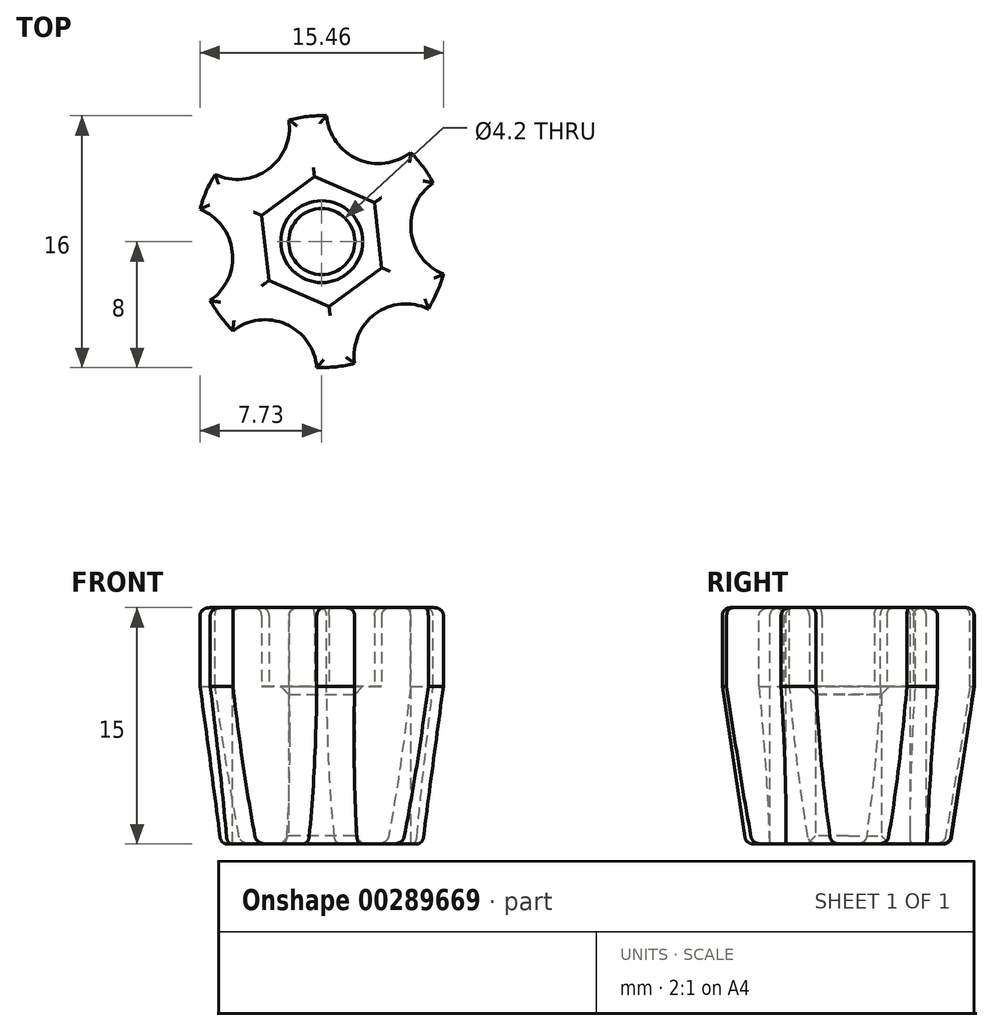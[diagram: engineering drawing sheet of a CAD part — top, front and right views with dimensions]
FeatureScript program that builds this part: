
annotation { "Feature Type Name" : "Feature", "Feature Type Description" : "" }
export const myFeature = defineFeature(function(context is Context, id is Id, definition is map)
    precondition{}
    {
        {
            var Q0;
            Q0=qCreatedBy(makeId("Top.planeOp"),FACE);
            var sketch = newSketch(context, id + "F0", { "sketchPlane" : qUnion([Q0])});
            skCircle(sketch, "E0", {"center": v(0, 0) * mm, "radius": 2.1 * mm});
            skCircle(sketch, "E1", {"center": v(0, 0) * mm, "radius": 6 * mm});
            skSolve(sketch);
        }
        {
            var Q0;
            Q0=makeQuery(id+"F0.imprint","IMPRINT",FACE,{"disambiguationData":[TD([[makeQuery(id+"F0.imprint","IMPRINT",EDGE,{"derivedFrom":sQuery(id+"F0.wireOp",EDGE,"E0")}),-1.0]])]});
            extrude(context, id + "F1", {"entities" : qUnion([Q0]), "depth" : 10 * mm});
        }
        {
            var Q0;
            Q0=qCreatedBy(makeId("Front.planeOp"),FACE);
            var sketch = newSketch(context, id + "F2", { "sketchPlane" : qUnion([Q0])});
            skLineSegment(sketch, "E2", {"start": v(0, 10) * mm, "end": v(0, 20) * mm});
            skLineSegment(sketch, "E3", {"start": v(0, 20) * mm, "end": v(8, 20) * mm});
            skLineSegment(sketch, "E4", {"start": v(8, 20) * mm, "end": v(0, 10) * mm});
            skLineSegment(sketch, "E5", {"start": v(0, 10) * mm, "end": v(6.5, 10) * mm});
            skLineSegment(sketch, "E6", {"start": v(6.5, 10) * mm, "end": v(8, 20) * mm});
            skLineSegment(sketch, "E7", {"start": v(0, 20) * mm, "end": v(2.1, 20) * mm});
            skLineSegment(sketch, "E8", {"start": v(2.1, 20) * mm, "end": v(2.1, 10) * mm});
            skSolve(sketch);
        }
        {
            var Q0;
            {var subQ0=sQuery(id+"F2.wireOp",EDGE,"E3");Q0=makeQuery(id+"F2.imprint","IMPRINT",FACE,{"disambiguationData":[TD([[makeQuery(id+"F2.imprint","IMPRINT",EDGE,{"derivedFrom":subQ0}),-1.0]])]});}
            var Q1;
            {var subQ0=sQuery(id+"F2.wireOp",EDGE,"E6");Q1=makeQuery(id+"F2.imprint","IMPRINT",FACE,{"disambiguationData":[TD([[makeQuery(id+"F2.imprint","IMPRINT",EDGE,{"derivedFrom":subQ0}),1.0]])]});}
            var Q2;
            Q2=sQuery(id+"F2.wireOp",EDGE,"E2");
            revolve(context, id + "F3", {"operationType" : NewBodyOperationType.ADD, "entities" : qUnion([Q0, Q1]), "axis" : qUnion([Q2]), "revolveType" : RevolveType.FULL});
        }
        {
            var Q0;
            Q0=makeQuery(id+"F3.opRevolve","SWEPT_FACE",FACE,{"disambiguationData":[OSD([sQuery(id+"F2.wireOp",EDGE,"E3")])]});
            var sketch = newSketch(context, id + "F4", { "sketchPlane" : qUnion([Q0])});
            skCircle(sketch, "E9.cCircle", {"center": v(0, 0) * mm, "radius": 5.25 * mm, "construction": true});
            skLineSegment(sketch, "E9.0", {"start": v(5.56, -2.42) * mm, "end": v(0.68, -6.02) * mm});
            skLineSegment(sketch, "E9.1", {"start": v(0.68, -6.02) * mm, "end": v(-4.88, -3.6) * mm});
            skLineSegment(sketch, "E9.2", {"start": v(-4.88, -3.6) * mm, "end": v(-5.56, 2.42) * mm});
            skLineSegment(sketch, "E9.3", {"start": v(-5.56, 2.42) * mm, "end": v(-0.68, 6.02) * mm});
            skLineSegment(sketch, "E9.4", {"start": v(-0.68, 6.02) * mm, "end": v(4.88, 3.6) * mm});
            skLineSegment(sketch, "E9.5", {"start": v(4.88, 3.6) * mm, "end": v(5.56, -2.42) * mm});
            skPoint(sketch, "E9.0.midPoint", {"position": v(3.12, -4.22) * mm});
            skCircle(sketch, "E10.cCircle", {"center": v(0, 0) * mm, "radius": 3.6 * mm, "construction": true});
            skLineSegment(sketch, "E10.0", {"start": v(-3.81, 1.66) * mm, "end": v(-0.47, 4.13) * mm});
            skLineSegment(sketch, "E10.1", {"start": v(-0.47, 4.13) * mm, "end": v(3.34, 2.47) * mm});
            skLineSegment(sketch, "E10.2", {"start": v(3.34, 2.47) * mm, "end": v(3.81, -1.66) * mm});
            skLineSegment(sketch, "E10.3", {"start": v(3.81, -1.66) * mm, "end": v(0.47, -4.13) * mm});
            skLineSegment(sketch, "E10.4", {"start": v(0.47, -4.13) * mm, "end": v(-3.34, -2.47) * mm});
            skLineSegment(sketch, "E10.5", {"start": v(-3.34, -2.47) * mm, "end": v(-3.81, 1.66) * mm});
            skPoint(sketch, "E10.0.midPoint", {"position": v(-2.14, 2.9) * mm});
            skSolve(sketch);
        }
        {
            var Q0;
            Q0=makeQuery(id+"F4.imprint","IMPRINT",FACE,{"disambiguationData":[TD([[makeQuery(id+"F4.imprint","IMPRINT",EDGE,{"derivedFrom":sQuery(id+"F4.wireOp",EDGE,"E9.0")}),1.0]])]});
            var Q1;
            Q1=makeQuery(id+"F4.imprint","IMPRINT",FACE,{"disambiguationData":[TD([[makeQuery(id+"F4.imprint","IMPRINT",EDGE,{"derivedFrom":sQuery(id+"F4.wireOp",EDGE,"E9.0")}),-1.0]])]});
            extrude(context, id + "F5", {"entities" : qUnion([Q0, Q1]), "operationType" : NewBodyOperationType.ADD, "depth" : 15 * mm});
        }
        {
            var Q0;
            Q0=makeQuery(id+"F5.opExtrude","CAP_FACE",FACE,{"disambiguationData":[OSD([sQuery(id+"F2.wireOp",EDGE,"E3"),sQuery(id+"F2.wireOp",EDGE,"E4"),sQuery(id+"F2.wireOp",EDGE,"E6"),sQuery(id+"F4.wireOp",EDGE,"E9.0"),sQuery(id+"F4.wireOp",EDGE,"E9.1"),sQuery(id+"F4.wireOp",EDGE,"E9.2"),sQuery(id+"F4.wireOp",EDGE,"E9.3"),sQuery(id+"F4.wireOp",EDGE,"E9.4"),sQuery(id+"F4.wireOp",EDGE,"E9.5")])],"isStart":false});
            var sketch = newSketch(context, id + "F6", { "sketchPlane" : qUnion([Q0])});
            skArc(sketch, "E11", {"start": v(1.44, 3.3) * mm, "mid": v(-0.92, 8.13) * mm, "end": v(-2.14, 2.9) * mm});
            skArc(sketch, "E12", {"start": v(-2.14, 2.9) * mm, "mid": v(-7.5, 3.27) * mm, "end": v(-3.58, -0.4) * mm});
            skArc(sketch, "E13", {"start": v(-6.77, 4.27) * mm, "mid": v(-3.4, 4.6) * mm, "end": v(-2.09, 7.72) * mm});
            skArc(sketch, "E14", {"start": v(-1.44, -3.3) * mm, "mid": v(0.92, -8.13) * mm, "end": v(2.14, -2.9) * mm});
            skArc(sketch, "E15", {"start": v(-3.58, -0.4) * mm, "mid": v(-6.58, -4.86) * mm, "end": v(-1.44, -3.3) * mm});
            skArc(sketch, "E16", {"start": v(2.14, -2.9) * mm, "mid": v(7.5, -3.27) * mm, "end": v(3.58, 0.4) * mm});
            skArc(sketch, "E17", {"start": v(3.58, 0.4) * mm, "mid": v(6.58, 4.86) * mm, "end": v(1.44, 3.3) * mm});
            skArc(sketch, "E18", {"start": v(0.32, 8) * mm, "mid": v(2.29, 5.24) * mm, "end": v(5.64, 5.67) * mm});
            skArc(sketch, "E19", {"start": v(7.08, 3.72) * mm, "mid": v(5.68, 0.64) * mm, "end": v(7.73, -2.05) * mm});
            skArc(sketch, "E20", {"start": v(6.77, -4.27) * mm, "mid": v(3.4, -4.6) * mm, "end": v(2.09, -7.72) * mm});
            skArc(sketch, "E21", {"start": v(-0.32, -8) * mm, "mid": v(-2.29, -5.24) * mm, "end": v(-5.64, -5.67) * mm});
            skArc(sketch, "E22", {"start": v(-7.08, -3.72) * mm, "mid": v(-5.68, -0.64) * mm, "end": v(-7.73, 2.05) * mm});
            skSolve(sketch);
        }
        {
            var Q0;
            {var subQ0=sQuery(id+"F6.wireOp",EDGE,"E13");var subQ1=sQuery(id+"F6.wireOp",EDGE,"E11");var subQ4=makeQuery(id+"F6.imprint","INTERSECT",VERTEX,{"derivedFrom":[subQ1,subQ0]});Q0=makeQuery(id+"F6.imprint","IMPRINT",FACE,{"disambiguationData":[TD([[makeQuery(id+"F6.imprint","IMPRINT",EDGE,{"disambiguationData":[TD([[subQ4,1.0]])],"derivedFrom":subQ0}),1.0]])]});}
            var Q1;
            {var subQ0=sQuery(id+"F6.wireOp",EDGE,"E13");var subQ1=sQuery(id+"F6.wireOp",EDGE,"E12");var subQ3=makeQuery(id+"F6.imprint","INTERSECT",VERTEX,{"derivedFrom":[subQ1,subQ0]});Q1=makeQuery(id+"F6.imprint","IMPRINT",FACE,{"disambiguationData":[TD([[makeQuery(id+"F6.imprint","IMPRINT",EDGE,{"disambiguationData":[TD([[subQ3,-1.0]])],"derivedFrom":subQ1}),1.0]])]});}
            var Q2;
            {var subQ0=sQuery(id+"F6.wireOp",EDGE,"E13");var subQ1=sQuery(id+"F6.wireOp",EDGE,"E11");var subQ3=makeQuery(id+"F6.imprint","INTERSECT",VERTEX,{"derivedFrom":[subQ1,subQ0]});Q2=makeQuery(id+"F6.imprint","IMPRINT",FACE,{"disambiguationData":[TD([[makeQuery(id+"F6.imprint","IMPRINT",EDGE,{"disambiguationData":[TD([[subQ3,1.0]])],"derivedFrom":subQ1}),1.0]])]});}
            var Q3;
            {var subQ0=sQuery(id+"F6.wireOp",EDGE,"E22");var subQ1=sQuery(id+"F6.wireOp",EDGE,"E12");var subQ4=makeQuery(id+"F6.imprint","INTERSECT",VERTEX,{"derivedFrom":[subQ1,subQ0]});Q3=makeQuery(id+"F6.imprint","IMPRINT",FACE,{"disambiguationData":[TD([[makeQuery(id+"F6.imprint","IMPRINT",EDGE,{"disambiguationData":[TD([[subQ4,1.0]])],"derivedFrom":subQ0}),1.0]])]});}
            var Q4;
            {var subQ0=sQuery(id+"F6.wireOp",EDGE,"E22");var subQ1=sQuery(id+"F6.wireOp",EDGE,"E12");var subQ3=makeQuery(id+"F6.imprint","INTERSECT",VERTEX,{"derivedFrom":[subQ1,subQ0]});Q4=makeQuery(id+"F6.imprint","IMPRINT",FACE,{"disambiguationData":[TD([[makeQuery(id+"F6.imprint","IMPRINT",EDGE,{"disambiguationData":[TD([[subQ3,1.0]])],"derivedFrom":subQ1}),1.0]])]});}
            var Q5;
            {var subQ0=sQuery(id+"F6.wireOp",EDGE,"E22");var subQ1=sQuery(id+"F6.wireOp",EDGE,"E15");var subQ3=makeQuery(id+"F6.imprint","INTERSECT",VERTEX,{"derivedFrom":[subQ1,subQ0]});Q5=makeQuery(id+"F6.imprint","IMPRINT",FACE,{"disambiguationData":[TD([[makeQuery(id+"F6.imprint","IMPRINT",EDGE,{"disambiguationData":[TD([[subQ3,-1.0]])],"derivedFrom":subQ1}),1.0]])]});}
            var Q6;
            {var subQ0=sQuery(id+"F6.wireOp",EDGE,"E21");var subQ1=sQuery(id+"F6.wireOp",EDGE,"E14");var subQ4=makeQuery(id+"F6.imprint","INTERSECT",VERTEX,{"derivedFrom":[subQ1,subQ0]});Q6=makeQuery(id+"F6.imprint","IMPRINT",FACE,{"disambiguationData":[TD([[makeQuery(id+"F6.imprint","IMPRINT",EDGE,{"disambiguationData":[TD([[subQ4,-1.0]])],"derivedFrom":subQ0}),1.0]])]});}
            var Q7;
            {var subQ0=sQuery(id+"F6.wireOp",EDGE,"E21");var subQ1=sQuery(id+"F6.wireOp",EDGE,"E15");var subQ3=makeQuery(id+"F6.imprint","INTERSECT",VERTEX,{"derivedFrom":[subQ1,subQ0]});Q7=makeQuery(id+"F6.imprint","IMPRINT",FACE,{"disambiguationData":[TD([[makeQuery(id+"F6.imprint","IMPRINT",EDGE,{"disambiguationData":[TD([[subQ3,1.0]])],"derivedFrom":subQ1}),1.0]])]});}
            var Q8;
            {var subQ0=sQuery(id+"F6.wireOp",EDGE,"E21");var subQ1=sQuery(id+"F6.wireOp",EDGE,"E14");var subQ3=makeQuery(id+"F6.imprint","INTERSECT",VERTEX,{"derivedFrom":[subQ1,subQ0]});Q8=makeQuery(id+"F6.imprint","IMPRINT",FACE,{"disambiguationData":[TD([[makeQuery(id+"F6.imprint","IMPRINT",EDGE,{"disambiguationData":[TD([[subQ3,-1.0]])],"derivedFrom":subQ1}),1.0]])]});}
            var Q9;
            {var subQ0=sQuery(id+"F6.wireOp",EDGE,"E20");var subQ1=sQuery(id+"F6.wireOp",EDGE,"E14");var subQ4=makeQuery(id+"F6.imprint","INTERSECT",VERTEX,{"derivedFrom":[subQ1,subQ0]});Q9=makeQuery(id+"F6.imprint","IMPRINT",FACE,{"disambiguationData":[TD([[makeQuery(id+"F6.imprint","IMPRINT",EDGE,{"disambiguationData":[TD([[subQ4,1.0]])],"derivedFrom":subQ0}),1.0]])]});}
            var Q10;
            {var subQ0=sQuery(id+"F6.wireOp",EDGE,"E20");var subQ1=sQuery(id+"F6.wireOp",EDGE,"E16");var subQ3=makeQuery(id+"F6.imprint","INTERSECT",VERTEX,{"derivedFrom":[subQ1,subQ0]});Q10=makeQuery(id+"F6.imprint","IMPRINT",FACE,{"disambiguationData":[TD([[makeQuery(id+"F6.imprint","IMPRINT",EDGE,{"disambiguationData":[TD([[subQ3,-1.0]])],"derivedFrom":subQ1}),1.0]])]});}
            var Q11;
            {var subQ0=sQuery(id+"F6.wireOp",EDGE,"E20");var subQ1=sQuery(id+"F6.wireOp",EDGE,"E14");var subQ3=makeQuery(id+"F6.imprint","INTERSECT",VERTEX,{"derivedFrom":[subQ1,subQ0]});Q11=makeQuery(id+"F6.imprint","IMPRINT",FACE,{"disambiguationData":[TD([[makeQuery(id+"F6.imprint","IMPRINT",EDGE,{"disambiguationData":[TD([[subQ3,1.0]])],"derivedFrom":subQ1}),1.0]])]});}
            var Q12;
            {var subQ0=sQuery(id+"F6.wireOp",EDGE,"E19");var subQ1=sQuery(id+"F6.wireOp",EDGE,"E16");var subQ4=makeQuery(id+"F6.imprint","INTERSECT",VERTEX,{"derivedFrom":[subQ1,subQ0]});Q12=makeQuery(id+"F6.imprint","IMPRINT",FACE,{"disambiguationData":[TD([[makeQuery(id+"F6.imprint","IMPRINT",EDGE,{"disambiguationData":[TD([[subQ4,1.0]])],"derivedFrom":subQ0}),1.0]])]});}
            var Q13;
            {var subQ0=sQuery(id+"F6.wireOp",EDGE,"E19");var subQ1=sQuery(id+"F6.wireOp",EDGE,"E16");var subQ3=makeQuery(id+"F6.imprint","INTERSECT",VERTEX,{"derivedFrom":[subQ1,subQ0]});Q13=makeQuery(id+"F6.imprint","IMPRINT",FACE,{"disambiguationData":[TD([[makeQuery(id+"F6.imprint","IMPRINT",EDGE,{"disambiguationData":[TD([[subQ3,1.0]])],"derivedFrom":subQ1}),1.0]])]});}
            var Q14;
            {var subQ0=sQuery(id+"F6.wireOp",EDGE,"E19");var subQ1=sQuery(id+"F6.wireOp",EDGE,"E17");var subQ3=makeQuery(id+"F6.imprint","INTERSECT",VERTEX,{"derivedFrom":[subQ1,subQ0]});Q14=makeQuery(id+"F6.imprint","IMPRINT",FACE,{"disambiguationData":[TD([[makeQuery(id+"F6.imprint","IMPRINT",EDGE,{"disambiguationData":[TD([[subQ3,-1.0]])],"derivedFrom":subQ1}),1.0]])]});}
            var Q15;
            {var subQ0=sQuery(id+"F6.wireOp",EDGE,"E18");var subQ1=sQuery(id+"F6.wireOp",EDGE,"E11");var subQ4=makeQuery(id+"F6.imprint","INTERSECT",VERTEX,{"derivedFrom":[subQ1,subQ0]});Q15=makeQuery(id+"F6.imprint","IMPRINT",FACE,{"disambiguationData":[TD([[makeQuery(id+"F6.imprint","IMPRINT",EDGE,{"disambiguationData":[TD([[subQ4,-1.0]])],"derivedFrom":subQ0}),1.0]])]});}
            var Q16;
            {var subQ0=sQuery(id+"F6.wireOp",EDGE,"E18");var subQ1=sQuery(id+"F6.wireOp",EDGE,"E11");var subQ3=makeQuery(id+"F6.imprint","INTERSECT",VERTEX,{"derivedFrom":[subQ1,subQ0]});Q16=makeQuery(id+"F6.imprint","IMPRINT",FACE,{"disambiguationData":[TD([[makeQuery(id+"F6.imprint","IMPRINT",EDGE,{"disambiguationData":[TD([[subQ3,-1.0]])],"derivedFrom":subQ1}),1.0]])]});}
            var Q17;
            {var subQ0=sQuery(id+"F6.wireOp",EDGE,"E18");var subQ1=sQuery(id+"F6.wireOp",EDGE,"E17");var subQ3=makeQuery(id+"F6.imprint","INTERSECT",VERTEX,{"derivedFrom":[subQ1,subQ0]});Q17=makeQuery(id+"F6.imprint","IMPRINT",FACE,{"disambiguationData":[TD([[makeQuery(id+"F6.imprint","IMPRINT",EDGE,{"disambiguationData":[TD([[subQ3,1.0]])],"derivedFrom":subQ1}),1.0]])]});}
            extrude(context, id + "F7", {"entities" : qUnion([Q0, Q1, Q2, Q3, Q4, Q5, Q6, Q7, Q8, Q9, Q10, Q11, Q12, Q13, Q14, Q15, Q16, Q17]), "operationType" : NewBodyOperationType.REMOVE, "oppositeDirection" : true, "depth" : 25 * mm});
        }
        {
            var Q0;
            Q0=makeQuery(id+"F5.opExtrude","CAP_FACE",FACE,{"disambiguationData":[OSD([sQuery(id+"F2.wireOp",EDGE,"E3"),sQuery(id+"F2.wireOp",EDGE,"E4"),sQuery(id+"F2.wireOp",EDGE,"E6"),sQuery(id+"F4.wireOp",EDGE,"E9.0"),sQuery(id+"F4.wireOp",EDGE,"E9.1"),sQuery(id+"F4.wireOp",EDGE,"E9.2"),sQuery(id+"F4.wireOp",EDGE,"E9.3"),sQuery(id+"F4.wireOp",EDGE,"E9.4"),sQuery(id+"F4.wireOp",EDGE,"E9.5")])],"isStart":false});
            extrude(context, id + "F8", {"entities" : qUnion([Q0]), "operationType" : NewBodyOperationType.REMOVE, "oppositeDirection" : true, "depth" : 5 * mm});
        }
        {
            var Q0;
            Q0=makeQuery(id+"F1.opExtrude","CAP_FACE",FACE,{"disambiguationData":[OSD([sQuery(id+"F0.wireOp",EDGE,"E0"),sQuery(id+"F0.wireOp",EDGE,"E1")])],"isStart":true});
            extrude(context, id + "F9", {"entities" : qUnion([Q0]), "operationType" : NewBodyOperationType.REMOVE, "oppositeDirection" : true, "depth" : 10 * mm});
        }
        {
            var Q0;
            Q0=makeQuery(id+"F8.boolean.opBoolean","COPY",FACE,{"derivedFrom":makeQuery(id+"F8.opExtrude","CAP_FACE",FACE,{"disambiguationData":[OSD([sQuery(id+"F2.wireOp",EDGE,"E3"),sQuery(id+"F2.wireOp",EDGE,"E4"),sQuery(id+"F2.wireOp",EDGE,"E6"),sQuery(id+"F4.wireOp",EDGE,"E10.0"),sQuery(id+"F4.wireOp",EDGE,"E10.1"),sQuery(id+"F4.wireOp",EDGE,"E10.2"),sQuery(id+"F4.wireOp",EDGE,"E10.3"),sQuery(id+"F4.wireOp",EDGE,"E10.4"),sQuery(id+"F4.wireOp",EDGE,"E10.5")])],"isStart":false})});
            extrude(context, id + "F10", {"entities" : qUnion([Q0]), "operationType" : NewBodyOperationType.REMOVE, "oppositeDirection" : true, "depth" : 5 * mm});
        }
        {
            var Q0;
            {var subQ0=sQuery(id+"F2.wireOp",EDGE,"E6");var subQ1=sQuery(id+"F2.wireOp",EDGE,"E4");var subQ2=sQuery(id+"F2.wireOp",EDGE,"E3");var subQ3=sQuery(id+"F6.wireOp",EDGE,"E21");var subQ5=makeQuery(id+"F5.opExtrude","CAP_EDGE",EDGE,{"disambiguationData":[OSD([subQ2,subQ1,subQ0])],"isStart":false});Q0=makeQuery(id+"F10.boolean.opBoolean","COPY",EDGE,{"derivedFrom":makeQuery(id+"F10.opExtrude","CAP_EDGE",EDGE,{"disambiguationData":[OSD([subQ2,subQ1,subQ0]),TDD([makeQuery(id+"F8.boolean.opBoolean","COPY",EDGE,{"derivedFrom":makeQuery(id+"F8.opExtrude","CAP_EDGE",EDGE,{"disambiguationData":[OSD([subQ2,subQ1,subQ0]),TDD([makeQuery(id+"F7.boolean.opBoolean","SPLIT",EDGE,{"disambiguationData":[TD([makeQuery(id+"F7.opExtrude","SWEPT_FACE",FACE,{"disambiguationData":[OSD([subQ3]),TDD([makeQuery(id+"F6.imprint","IMPRINT",EDGE,{"disambiguationData":[TD([[makeQuery(id+"F6.imprint","INTERSECT",VERTEX,{"derivedFrom":[sQuery(id+"F6.wireOp",EDGE,"E14"),subQ3]}),-1.0]])],"derivedFrom":subQ3})])]})])],"derivedFrom":subQ5})])],"isStart":false})})])],"isStart":false})});}
            var Q1;
            {var subQ0=sQuery(id+"F2.wireOp",EDGE,"E6");var subQ1=sQuery(id+"F2.wireOp",EDGE,"E4");var subQ2=sQuery(id+"F2.wireOp",EDGE,"E3");var subQ3=sQuery(id+"F6.wireOp",EDGE,"E20");var subQ5=makeQuery(id+"F5.opExtrude","CAP_EDGE",EDGE,{"disambiguationData":[OSD([subQ2,subQ1,subQ0])],"isStart":false});Q1=makeQuery(id+"F10.boolean.opBoolean","COPY",EDGE,{"derivedFrom":makeQuery(id+"F10.opExtrude","CAP_EDGE",EDGE,{"disambiguationData":[OSD([subQ2,subQ1,subQ0]),TDD([makeQuery(id+"F8.boolean.opBoolean","COPY",EDGE,{"derivedFrom":makeQuery(id+"F8.opExtrude","CAP_EDGE",EDGE,{"disambiguationData":[OSD([subQ2,subQ1,subQ0]),TDD([makeQuery(id+"F7.boolean.opBoolean","SPLIT",EDGE,{"disambiguationData":[TD([makeQuery(id+"F7.opExtrude","SWEPT_FACE",FACE,{"disambiguationData":[OSD([subQ3]),TDD([makeQuery(id+"F6.imprint","IMPRINT",EDGE,{"disambiguationData":[TD([[makeQuery(id+"F6.imprint","INTERSECT",VERTEX,{"derivedFrom":[sQuery(id+"F6.wireOp",EDGE,"E16"),subQ3]}),-1.0]])],"derivedFrom":subQ3})])]})])],"derivedFrom":subQ5})])],"isStart":false})})])],"isStart":false})});}
            var Q2;
            {var subQ0=sQuery(id+"F2.wireOp",EDGE,"E6");var subQ1=sQuery(id+"F2.wireOp",EDGE,"E4");var subQ2=sQuery(id+"F2.wireOp",EDGE,"E3");var subQ3=sQuery(id+"F6.wireOp",EDGE,"E19");var subQ5=makeQuery(id+"F5.opExtrude","CAP_EDGE",EDGE,{"disambiguationData":[OSD([subQ2,subQ1,subQ0])],"isStart":false});Q2=makeQuery(id+"F10.boolean.opBoolean","COPY",EDGE,{"derivedFrom":makeQuery(id+"F10.opExtrude","CAP_EDGE",EDGE,{"disambiguationData":[OSD([subQ2,subQ1,subQ0]),TDD([makeQuery(id+"F8.boolean.opBoolean","COPY",EDGE,{"derivedFrom":makeQuery(id+"F8.opExtrude","CAP_EDGE",EDGE,{"disambiguationData":[OSD([subQ2,subQ1,subQ0]),TDD([makeQuery(id+"F7.boolean.opBoolean","SPLIT",EDGE,{"disambiguationData":[TD([makeQuery(id+"F7.opExtrude","SWEPT_FACE",FACE,{"disambiguationData":[OSD([subQ3]),TDD([makeQuery(id+"F6.imprint","IMPRINT",EDGE,{"disambiguationData":[TD([[makeQuery(id+"F6.imprint","INTERSECT",VERTEX,{"derivedFrom":[sQuery(id+"F6.wireOp",EDGE,"E17"),subQ3]}),-1.0]])],"derivedFrom":subQ3})])]})])],"derivedFrom":subQ5})])],"isStart":false})})])],"isStart":false})});}
            var Q3;
            {var subQ0=sQuery(id+"F2.wireOp",EDGE,"E6");var subQ1=sQuery(id+"F2.wireOp",EDGE,"E4");var subQ2=sQuery(id+"F2.wireOp",EDGE,"E3");var subQ5=makeQuery(id+"F5.opExtrude","CAP_EDGE",EDGE,{"disambiguationData":[OSD([subQ2,subQ1,subQ0])],"isStart":false});var subQ6=sQuery(id+"F6.wireOp",EDGE,"E18");Q3=makeQuery(id+"F10.boolean.opBoolean","COPY",EDGE,{"derivedFrom":makeQuery(id+"F10.opExtrude","CAP_EDGE",EDGE,{"disambiguationData":[OSD([subQ2,subQ1,subQ0]),TDD([makeQuery(id+"F8.boolean.opBoolean","COPY",EDGE,{"derivedFrom":makeQuery(id+"F8.opExtrude","CAP_EDGE",EDGE,{"disambiguationData":[OSD([subQ2,subQ1,subQ0]),TDD([makeQuery(id+"F7.boolean.opBoolean","SPLIT",EDGE,{"disambiguationData":[TD([makeQuery(id+"F7.opExtrude","SWEPT_FACE",FACE,{"disambiguationData":[OSD([subQ6]),TDD([makeQuery(id+"F6.imprint","IMPRINT",EDGE,{"disambiguationData":[TD([[makeQuery(id+"F6.imprint","INTERSECT",VERTEX,{"derivedFrom":[sQuery(id+"F6.wireOp",EDGE,"E11"),subQ6]}),-1.0]])],"derivedFrom":subQ6})])]})])],"derivedFrom":subQ5})])],"isStart":false})})])],"isStart":false})});}
            var Q4;
            {var subQ0=sQuery(id+"F2.wireOp",EDGE,"E6");var subQ1=sQuery(id+"F2.wireOp",EDGE,"E4");var subQ2=sQuery(id+"F2.wireOp",EDGE,"E3");var subQ3=sQuery(id+"F6.wireOp",EDGE,"E13");var subQ5=makeQuery(id+"F5.opExtrude","CAP_EDGE",EDGE,{"disambiguationData":[OSD([subQ2,subQ1,subQ0])],"isStart":false});Q4=makeQuery(id+"F10.boolean.opBoolean","COPY",EDGE,{"derivedFrom":makeQuery(id+"F10.opExtrude","CAP_EDGE",EDGE,{"disambiguationData":[OSD([subQ2,subQ1,subQ0]),TDD([makeQuery(id+"F8.boolean.opBoolean","COPY",EDGE,{"derivedFrom":makeQuery(id+"F8.opExtrude","CAP_EDGE",EDGE,{"disambiguationData":[OSD([subQ2,subQ1,subQ0]),TDD([makeQuery(id+"F7.boolean.opBoolean","SPLIT",EDGE,{"disambiguationData":[TD([makeQuery(id+"F7.opExtrude","SWEPT_FACE",FACE,{"disambiguationData":[OSD([subQ3]),TDD([makeQuery(id+"F6.imprint","IMPRINT",EDGE,{"disambiguationData":[TD([[makeQuery(id+"F6.imprint","INTERSECT",VERTEX,{"derivedFrom":[sQuery(id+"F6.wireOp",EDGE,"E12"),subQ3]}),-1.0]])],"derivedFrom":subQ3})])]})])],"derivedFrom":subQ5})])],"isStart":false})})])],"isStart":false})});}
            var Q5;
            {var subQ0=sQuery(id+"F2.wireOp",EDGE,"E6");var subQ1=sQuery(id+"F2.wireOp",EDGE,"E4");var subQ2=sQuery(id+"F2.wireOp",EDGE,"E3");var subQ3=sQuery(id+"F6.wireOp",EDGE,"E13");var subQ5=makeQuery(id+"F5.opExtrude","CAP_EDGE",EDGE,{"disambiguationData":[OSD([subQ2,subQ1,subQ0])],"isStart":false});Q5=makeQuery(id+"F10.boolean.opBoolean","COPY",EDGE,{"derivedFrom":makeQuery(id+"F10.opExtrude","CAP_EDGE",EDGE,{"disambiguationData":[OSD([subQ2,subQ1,subQ0]),TDD([makeQuery(id+"F8.boolean.opBoolean","COPY",EDGE,{"derivedFrom":makeQuery(id+"F8.opExtrude","CAP_EDGE",EDGE,{"disambiguationData":[OSD([subQ2,subQ1,subQ0]),TDD([makeQuery(id+"F7.boolean.opBoolean","SPLIT",EDGE,{"disambiguationData":[TD([makeQuery(id+"F7.opExtrude","SWEPT_FACE",FACE,{"disambiguationData":[OSD([subQ3]),TDD([makeQuery(id+"F6.imprint","IMPRINT",EDGE,{"disambiguationData":[TD([[makeQuery(id+"F6.imprint","INTERSECT",VERTEX,{"derivedFrom":[sQuery(id+"F6.wireOp",EDGE,"E11"),subQ3]}),1.0]])],"derivedFrom":subQ3})])]})])],"derivedFrom":subQ5})])],"isStart":false})})])],"isStart":false})});}
            var Q6;
            Q6=makeQuery(id+"F10.boolean.opBoolean","COPY",EDGE,{"derivedFrom":makeQuery(id+"F10.opExtrude","CAP_EDGE",EDGE,{"disambiguationData":[OSD([sQuery(id+"F6.wireOp",EDGE,"E21")])],"isStart":false})});
            var Q7;
            Q7=makeQuery(id+"F10.boolean.opBoolean","COPY",FACE,{"derivedFrom":makeQuery(id+"F10.opExtrude","CAP_FACE",FACE,{"disambiguationData":[OSD([sQuery(id+"F2.wireOp",EDGE,"E3"),sQuery(id+"F2.wireOp",EDGE,"E4"),sQuery(id+"F2.wireOp",EDGE,"E6"),sQuery(id+"F4.wireOp",EDGE,"E10.0"),sQuery(id+"F4.wireOp",EDGE,"E10.1"),sQuery(id+"F4.wireOp",EDGE,"E10.2"),sQuery(id+"F4.wireOp",EDGE,"E10.3"),sQuery(id+"F4.wireOp",EDGE,"E10.4"),sQuery(id+"F4.wireOp",EDGE,"E10.5")])],"isStart":false})});
            fillet(context, id + "F11", {"entities" : qUnion([Q0, Q1, Q2, Q3, Q4, Q5, Q6, Q7]), "radius" : 0.5 * mm, "tangentPropagation" : true, "allowEdgeOverflow" : false});
        }
        {
            var Q0;
            Q0=makeQuery(id+"F3.boolean.opBoolean","MERGE",FACE,{"derivedFrom":[makeQuery(id+"F1.opExtrude","SWEPT_FACE",FACE,{"disambiguationData":[OSD([sQuery(id+"F0.wireOp",EDGE,"E0")])]}),makeQuery(id+"F3.opRevolve","SWEPT_FACE",FACE,{"disambiguationData":[OSD([sQuery(id+"F2.wireOp",EDGE,"E8")])]})]});
            chamfer(context, id + "F12", {"entities" : qUnion([Q0]), "width" : 0.5 * mm, "tangentPropagation" : true});
        }
        {
            var Q0;
            {var subQ0=sQuery(id+"F2.wireOp",EDGE,"E5");var subQ1=sQuery(id+"F2.wireOp",EDGE,"E6");Q0=makeQuery(id+"F7.boolean.opBoolean","SPLIT",EDGE,{"disambiguationData":[TD([makeQuery(id+"F3.opRevolve","SWEPT_FACE",FACE,{"disambiguationData":[OSD([subQ0])]}),makeQuery(id+"F3.opRevolve","SWEPT_FACE",FACE,{"disambiguationData":[OSD([subQ1])]}),makeQuery(id+"F7.opExtrude","SWEPT_FACE",FACE,{"disambiguationData":[OSD([sQuery(id+"F6.wireOp",EDGE,"E13")])]}),makeQuery(id+"F7.opExtrude","SWEPT_FACE",FACE,{"disambiguationData":[OSD([sQuery(id+"F6.wireOp",EDGE,"E18")])]})])],"derivedFrom":makeQuery(id+"F3.opRevolve","SWEPT_EDGE",EDGE,{"disambiguationData":[OSD([subQ0,subQ1])]})});}
            var Q1;
            {var subQ0=sQuery(id+"F2.wireOp",EDGE,"E5");var subQ1=sQuery(id+"F2.wireOp",EDGE,"E6");Q1=makeQuery(id+"F7.boolean.opBoolean","SPLIT",EDGE,{"disambiguationData":[TD([makeQuery(id+"F3.opRevolve","SWEPT_FACE",FACE,{"disambiguationData":[OSD([subQ0])]}),makeQuery(id+"F3.opRevolve","SWEPT_FACE",FACE,{"disambiguationData":[OSD([subQ1])]}),makeQuery(id+"F7.opExtrude","SWEPT_FACE",FACE,{"disambiguationData":[OSD([sQuery(id+"F6.wireOp",EDGE,"E18")])]}),makeQuery(id+"F7.opExtrude","SWEPT_FACE",FACE,{"disambiguationData":[OSD([sQuery(id+"F6.wireOp",EDGE,"E19")])]})])],"derivedFrom":makeQuery(id+"F3.opRevolve","SWEPT_EDGE",EDGE,{"disambiguationData":[OSD([subQ0,subQ1])]})});}
            var Q2;
            {var subQ0=sQuery(id+"F2.wireOp",EDGE,"E5");var subQ1=sQuery(id+"F2.wireOp",EDGE,"E6");Q2=makeQuery(id+"F7.boolean.opBoolean","SPLIT",EDGE,{"disambiguationData":[TD([makeQuery(id+"F3.opRevolve","SWEPT_FACE",FACE,{"disambiguationData":[OSD([subQ0])]}),makeQuery(id+"F3.opRevolve","SWEPT_FACE",FACE,{"disambiguationData":[OSD([subQ1])]}),makeQuery(id+"F7.opExtrude","SWEPT_FACE",FACE,{"disambiguationData":[OSD([sQuery(id+"F6.wireOp",EDGE,"E13")])]}),makeQuery(id+"F7.opExtrude","SWEPT_FACE",FACE,{"disambiguationData":[OSD([sQuery(id+"F6.wireOp",EDGE,"E22")])]})])],"derivedFrom":makeQuery(id+"F3.opRevolve","SWEPT_EDGE",EDGE,{"disambiguationData":[OSD([subQ0,subQ1])]})});}
            var Q3;
            {var subQ0=sQuery(id+"F2.wireOp",EDGE,"E5");var subQ1=sQuery(id+"F2.wireOp",EDGE,"E6");Q3=makeQuery(id+"F7.boolean.opBoolean","SPLIT",EDGE,{"disambiguationData":[TD([makeQuery(id+"F3.opRevolve","SWEPT_FACE",FACE,{"disambiguationData":[OSD([subQ0])]}),makeQuery(id+"F3.opRevolve","SWEPT_FACE",FACE,{"disambiguationData":[OSD([subQ1])]}),makeQuery(id+"F7.opExtrude","SWEPT_FACE",FACE,{"disambiguationData":[OSD([sQuery(id+"F6.wireOp",EDGE,"E21")])]}),makeQuery(id+"F7.opExtrude","SWEPT_FACE",FACE,{"disambiguationData":[OSD([sQuery(id+"F6.wireOp",EDGE,"E22")])]})])],"derivedFrom":makeQuery(id+"F3.opRevolve","SWEPT_EDGE",EDGE,{"disambiguationData":[OSD([subQ0,subQ1])]})});}
            var Q4;
            {var subQ0=sQuery(id+"F2.wireOp",EDGE,"E5");var subQ1=sQuery(id+"F2.wireOp",EDGE,"E6");Q4=makeQuery(id+"F7.boolean.opBoolean","SPLIT",EDGE,{"disambiguationData":[TD([makeQuery(id+"F3.opRevolve","SWEPT_FACE",FACE,{"disambiguationData":[OSD([subQ0])]}),makeQuery(id+"F3.opRevolve","SWEPT_FACE",FACE,{"disambiguationData":[OSD([subQ1])]}),makeQuery(id+"F7.opExtrude","SWEPT_FACE",FACE,{"disambiguationData":[OSD([sQuery(id+"F6.wireOp",EDGE,"E20")])]}),makeQuery(id+"F7.opExtrude","SWEPT_FACE",FACE,{"disambiguationData":[OSD([sQuery(id+"F6.wireOp",EDGE,"E21")])]})])],"derivedFrom":makeQuery(id+"F3.opRevolve","SWEPT_EDGE",EDGE,{"disambiguationData":[OSD([subQ0,subQ1])]})});}
            var Q5;
            {var subQ0=sQuery(id+"F2.wireOp",EDGE,"E5");var subQ1=sQuery(id+"F2.wireOp",EDGE,"E6");Q5=makeQuery(id+"F7.boolean.opBoolean","SPLIT",EDGE,{"disambiguationData":[TD([makeQuery(id+"F3.opRevolve","SWEPT_FACE",FACE,{"disambiguationData":[OSD([subQ0])]}),makeQuery(id+"F3.opRevolve","SWEPT_FACE",FACE,{"disambiguationData":[OSD([subQ1])]}),makeQuery(id+"F7.opExtrude","SWEPT_FACE",FACE,{"disambiguationData":[OSD([sQuery(id+"F6.wireOp",EDGE,"E19")])]}),makeQuery(id+"F7.opExtrude","SWEPT_FACE",FACE,{"disambiguationData":[OSD([sQuery(id+"F6.wireOp",EDGE,"E20")])]})])],"derivedFrom":makeQuery(id+"F3.opRevolve","SWEPT_EDGE",EDGE,{"disambiguationData":[OSD([subQ0,subQ1])]})});}
            var Q6;
            {var subQ0=sQuery(id+"F6.wireOp",EDGE,"E22");Q6=makeQuery(id+"F7.boolean.opBoolean","COPY",EDGE,{"disambiguationData":[topologyDisambiguationEdgeConnected([makeQuery(id+"F7.opExtrude","SWEPT_FACE",FACE,{"disambiguationData":[OSD([subQ0])]}),makeQuery(id+"F7.opExtrude","CAP_FACE",FACE,{"disambiguationData":[OSD([sQuery(id+"F2.wireOp",EDGE,"E3"),sQuery(id+"F2.wireOp",EDGE,"E4"),sQuery(id+"F2.wireOp",EDGE,"E6"),subQ0])],"isStart":false})])],"derivedFrom":makeQuery(id+"F7.opExtrude","CAP_EDGE",EDGE,{"disambiguationData":[OSD([subQ0])],"isStart":false})});}
            var Q7;
            {var subQ0=sQuery(id+"F6.wireOp",EDGE,"E21");Q7=makeQuery(id+"F7.boolean.opBoolean","COPY",EDGE,{"disambiguationData":[topologyDisambiguationEdgeConnected([makeQuery(id+"F7.opExtrude","SWEPT_FACE",FACE,{"disambiguationData":[OSD([subQ0])]}),makeQuery(id+"F7.opExtrude","CAP_FACE",FACE,{"disambiguationData":[OSD([sQuery(id+"F2.wireOp",EDGE,"E3"),sQuery(id+"F2.wireOp",EDGE,"E4"),sQuery(id+"F2.wireOp",EDGE,"E6"),subQ0])],"isStart":false})])],"derivedFrom":makeQuery(id+"F7.opExtrude","CAP_EDGE",EDGE,{"disambiguationData":[OSD([subQ0])],"isStart":false})});}
            var Q8;
            {var subQ0=sQuery(id+"F6.wireOp",EDGE,"E20");Q8=makeQuery(id+"F7.boolean.opBoolean","COPY",EDGE,{"disambiguationData":[topologyDisambiguationEdgeConnected([makeQuery(id+"F7.opExtrude","SWEPT_FACE",FACE,{"disambiguationData":[OSD([subQ0])]}),makeQuery(id+"F7.opExtrude","CAP_FACE",FACE,{"disambiguationData":[OSD([sQuery(id+"F2.wireOp",EDGE,"E3"),sQuery(id+"F2.wireOp",EDGE,"E4"),sQuery(id+"F2.wireOp",EDGE,"E6"),subQ0])],"isStart":false})])],"derivedFrom":makeQuery(id+"F7.opExtrude","CAP_EDGE",EDGE,{"disambiguationData":[OSD([subQ0])],"isStart":false})});}
            var Q9;
            {var subQ0=sQuery(id+"F6.wireOp",EDGE,"E19");Q9=makeQuery(id+"F7.boolean.opBoolean","COPY",EDGE,{"disambiguationData":[topologyDisambiguationEdgeConnected([makeQuery(id+"F7.opExtrude","SWEPT_FACE",FACE,{"disambiguationData":[OSD([subQ0])]}),makeQuery(id+"F7.opExtrude","CAP_FACE",FACE,{"disambiguationData":[OSD([sQuery(id+"F2.wireOp",EDGE,"E3"),sQuery(id+"F2.wireOp",EDGE,"E4"),sQuery(id+"F2.wireOp",EDGE,"E6"),subQ0])],"isStart":false})])],"derivedFrom":makeQuery(id+"F7.opExtrude","CAP_EDGE",EDGE,{"disambiguationData":[OSD([subQ0])],"isStart":false})});}
            var Q10;
            {var subQ0=sQuery(id+"F6.wireOp",EDGE,"E18");Q10=makeQuery(id+"F7.boolean.opBoolean","COPY",EDGE,{"disambiguationData":[topologyDisambiguationEdgeConnected([makeQuery(id+"F7.opExtrude","SWEPT_FACE",FACE,{"disambiguationData":[OSD([subQ0])]}),makeQuery(id+"F7.opExtrude","CAP_FACE",FACE,{"disambiguationData":[OSD([sQuery(id+"F2.wireOp",EDGE,"E3"),sQuery(id+"F2.wireOp",EDGE,"E4"),sQuery(id+"F2.wireOp",EDGE,"E6"),subQ0])],"isStart":false})])],"derivedFrom":makeQuery(id+"F7.opExtrude","CAP_EDGE",EDGE,{"disambiguationData":[OSD([subQ0])],"isStart":false})});}
            var Q11;
            {var subQ0=sQuery(id+"F6.wireOp",EDGE,"E13");Q11=makeQuery(id+"F7.boolean.opBoolean","COPY",EDGE,{"disambiguationData":[topologyDisambiguationEdgeConnected([makeQuery(id+"F7.opExtrude","SWEPT_FACE",FACE,{"disambiguationData":[OSD([subQ0])]}),makeQuery(id+"F7.opExtrude","CAP_FACE",FACE,{"disambiguationData":[OSD([sQuery(id+"F2.wireOp",EDGE,"E3"),sQuery(id+"F2.wireOp",EDGE,"E4"),sQuery(id+"F2.wireOp",EDGE,"E6"),subQ0])],"isStart":false})])],"derivedFrom":makeQuery(id+"F7.opExtrude","CAP_EDGE",EDGE,{"disambiguationData":[OSD([subQ0])],"isStart":false})});}
            fillet(context, id + "F13", {"entities" : qUnion([Q0, Q1, Q2, Q3, Q4, Q5, Q6, Q7, Q8, Q9, Q10, Q11]), "radius" : 0.5 * mm, "tangentPropagation" : true, "allowEdgeOverflow" : false});
        }
    });
